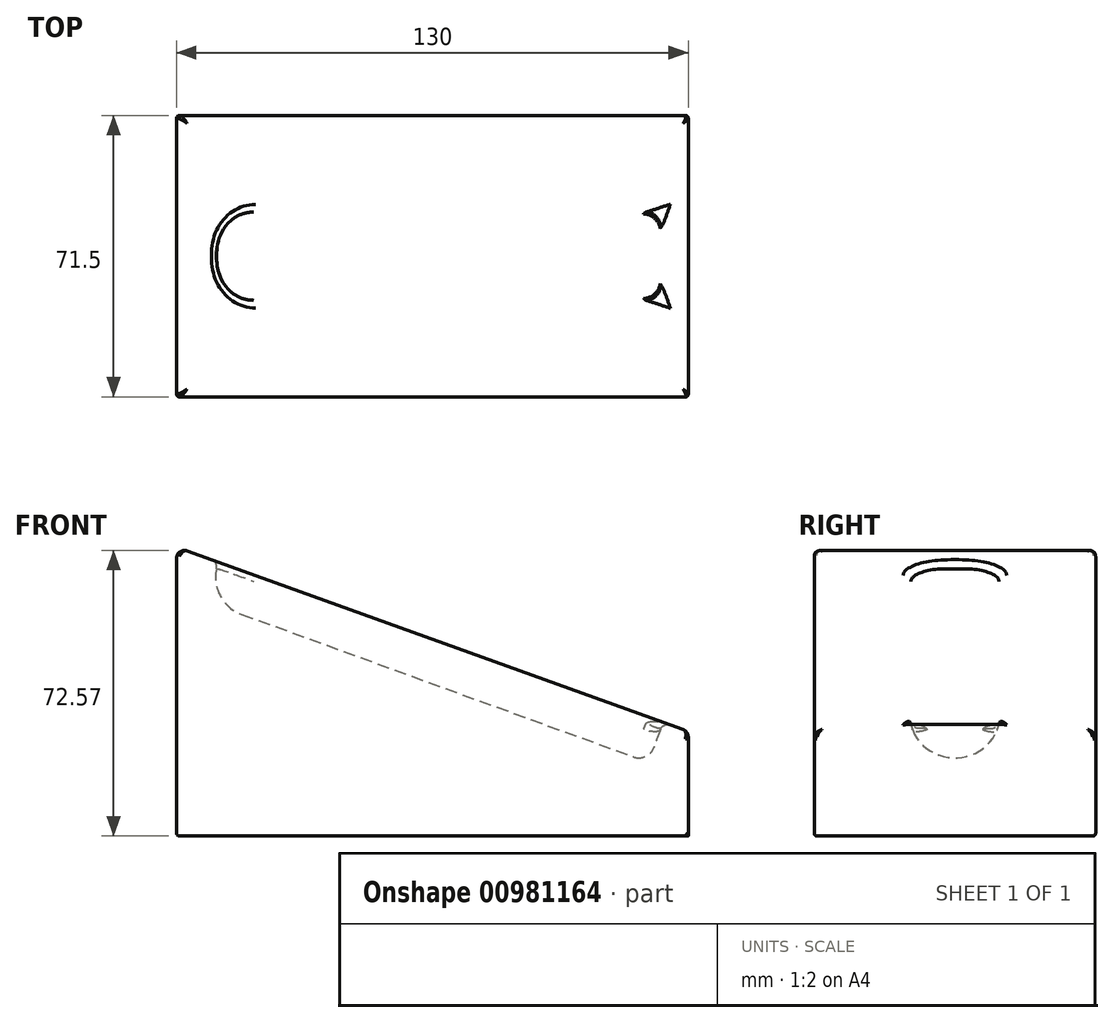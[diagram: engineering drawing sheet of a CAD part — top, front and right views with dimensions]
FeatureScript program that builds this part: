
annotation { "Feature Type Name" : "Feature", "Feature Type Description" : "" }
export const myFeature = defineFeature(function(context is Context, id is Id, definition is map)
    precondition{}
    {
        {
            var Q0;
            Q0=qCreatedBy(makeId("Top.planeOp"),FACE);
            var sketch = newSketch(context, id + "F0", { "sketchPlane" : qUnion([Q0])});
            skLineSegment(sketch, "E0.bottom", {"start": v(0, 0) * mm, "end": v(130, 0) * mm});
            skLineSegment(sketch, "E0.top", {"start": v(0, -71.5) * mm, "end": v(130, -71.5) * mm});
            skLineSegment(sketch, "E0.left", {"start": v(0, 0) * mm, "end": v(0, -71.5) * mm});
            skLineSegment(sketch, "E0.right", {"start": v(130, 0) * mm, "end": v(130, -71.5) * mm});
            skSolve(sketch);
        }
        {
            var Q0;
            Q0=makeQuery(id+"F0.imprint","IMPRINT",FACE,{"disambiguationData":[TD([[makeQuery(id+"F0.imprint","IMPRINT",EDGE,{"derivedFrom":sQuery(id+"F0.wireOp",EDGE,"E0.bottom")}),-1.0]])]});
            extrude(context, id + "F1", {"entities" : qUnion([Q0]), "depth" : 77 * mm, "offsetDistance" : 25 * mm});
        }
        {
            var Q0;
            Q0=makeQuery(id+"F1.opExtrude","SWEPT_FACE",FACE,{"disambiguationData":[OSD([sQuery(id+"F0.wireOp",EDGE,"E0.top")])]});
            var sketch = newSketch(context, id + "F2", { "sketchPlane" : qUnion([Q0])});
            skLineSegment(sketch, "E1", {"start": v(0, 73.42) * mm, "end": v(130, 26.58) * mm});
            skLineSegment(sketch, "E2", {"start": v(130, 26.58) * mm, "end": v(130, 77) * mm});
            skLineSegment(sketch, "E3", {"start": v(130, 77) * mm, "end": v(0, 77) * mm});
            skLineSegment(sketch, "E4", {"start": v(0, 77) * mm, "end": v(0, 73.42) * mm});
            skSolve(sketch);
        }
        {
            var Q0;
            Q0=makeQuery(id+"F2.imprint","IMPRINT",FACE,{"disambiguationData":[TD([[makeQuery(id+"F2.imprint","IMPRINT",EDGE,{"derivedFrom":sQuery(id+"F2.wireOp",EDGE,"E1")}),1.0]])]});
            extrude(context, id + "F3", {"entities" : qUnion([Q0]), "operationType" : NewBodyOperationType.REMOVE, "endBound" : BoundingType.THROUGH_ALL, "oppositeDirection" : true, "depth" : 25 * mm, "offsetDistance" : 25 * mm});
        }
        {
            var Q0;
            Q0=makeQuery(id+"F1.opExtrude","SWEPT_FACE",FACE,{"disambiguationData":[OSD([sQuery(id+"F0.wireOp",EDGE,"E0.right")])]});
            var sketch = newSketch(context, id + "F4", { "sketchPlane" : qUnion([Q0])});
            skArc(sketch, "E5", {"start": v(-47.25, 26.58) * mm, "mid": v(-35.75, 15.08) * mm, "end": v(-24.25, 26.58) * mm});
            skSolve(sketch);
        }
        {
            var Q0;
            Q0 = qSketchRegion(id + "F4", true);
            var Q1;
            {var subQ0=sQuery(id+"F4.wireOp",EDGE,"E5");Q1=makeQuery(id+"F4.imprint","IMPRINT",FACE,{"disambiguationData":[TD([[makeQuery(id+"F4.imprint","IMPRINT",EDGE,{"derivedFrom":subQ0}),1.0]])]});}
            extrude(context, id + "F5", {"entities" : qUnion([Q0, Q1]), "operationType" : NewBodyOperationType.ADD, "depth" : 25 * mm, "offsetDistance" : 25 * mm});
        }
        {
            var Q0;
            Q0=makeQuery(id+"F5.opExtrude","CAP_FACE",FACE,{"disambiguationData":[OSD([sQuery(id+"F0.wireOp",EDGE,"E0.top"),sQuery(id+"F0.wireOp",EDGE,"E0.right"),sQuery(id+"F2.wireOp",EDGE,"E1"),sQuery(id+"F2.wireOp",EDGE,"E2"),sQuery(id+"F4.wireOp",EDGE,"E5")])],"isStart":false});
            extrude(context, id + "F6", {"entities" : qUnion([Q0]), "oppositeDirection" : true, "depth" : 120 * mm, "offsetDistance" : 25 * mm});
        }
        {
            var Q0;
            Q0=makeQuery(id+"F6.opExtrude","SWEPT_BODY",BODY,{"disambiguationData":[OSD([sQuery(id+"F0.wireOp",EDGE,"E0.top"),sQuery(id+"F0.wireOp",EDGE,"E0.right"),sQuery(id+"F2.wireOp",EDGE,"E1"),sQuery(id+"F2.wireOp",EDGE,"E2"),sQuery(id+"F4.wireOp",EDGE,"E5")])]});
            var Q1;
            {var subQ0=sQuery(id+"F2.wireOp",EDGE,"E2");var subQ1=sQuery(id+"F2.wireOp",EDGE,"E1");var subQ2=sQuery(id+"F0.wireOp",EDGE,"E0.right");var subQ3=sQuery(id+"F0.wireOp",EDGE,"E0.top");Q1=makeQuery(id+"F5.boolean.opBoolean","MERGE",EDGE,{"derivedFrom":[makeQuery(id+"F3.boolean.opBoolean","COPY",EDGE,{"derivedFrom":makeQuery(id+"F3.opExtrude","SWEPT_EDGE",EDGE,{"disambiguationData":[OSD([subQ3,subQ2,subQ1,subQ0])]})}),makeQuery(id+"F5.opExtrude","CAP_EDGE",EDGE,{"disambiguationData":[OSD([subQ3,subQ2,subQ1,subQ0])],"isStart":true})]});}
            transform(context, id + "F7", {"entities" : qUnion([Q0]), "transformType" : TransformType.ROTATION, "transformAxis" : qUnion([Q1]), "angle" : 20 * degree, "oppositeDirection" : true, "makeCopy" : false});
        }
        {
            var Q0;
            Q0=makeQuery(id+"F6.opExtrude","SWEPT_BODY",BODY,{"disambiguationData":[OSD([sQuery(id+"F0.wireOp",EDGE,"E0.top"),sQuery(id+"F0.wireOp",EDGE,"E0.right"),sQuery(id+"F2.wireOp",EDGE,"E1"),sQuery(id+"F2.wireOp",EDGE,"E2"),sQuery(id+"F4.wireOp",EDGE,"E5")])]});
            transform(context, id + "F8", {"entities" : qUnion([Q0]), "transformType" : TransformType.TRANSLATION_3D, "dx" : -29.7 * mm, "dy" : 0 * mm, "dz" : 11.5 * mm, "makeCopy" : false});
        }
        {
            var Q0;
            Q0=makeQuery(id+"F6.opExtrude","SWEPT_BODY",BODY,{"disambiguationData":[OSD([sQuery(id+"F0.wireOp",EDGE,"E0.top"),sQuery(id+"F0.wireOp",EDGE,"E0.right"),sQuery(id+"F2.wireOp",EDGE,"E1"),sQuery(id+"F2.wireOp",EDGE,"E2"),sQuery(id+"F4.wireOp",EDGE,"E5")])]});
            var Q1;
            Q1=makeQuery(id+"F1.opExtrude","SWEPT_BODY",BODY,{"disambiguationData":[OSD([sQuery(id+"F0.wireOp",EDGE,"E0.bottom"),sQuery(id+"F0.wireOp",EDGE,"E0.top"),sQuery(id+"F0.wireOp",EDGE,"E0.left"),sQuery(id+"F0.wireOp",EDGE,"E0.right")])]});
            booleanBodies(context, id + "F9", {"operationType" : BooleanOperationType.SUBTRACTION, "tools" : qUnion([Q0]), "targets" : qUnion([Q1])});
        }
        {
            var Q0;
            Q0=makeQuery(id+"F1.opExtrude","CAP_FACE",FACE,{"disambiguationData":[OSD([sQuery(id+"F0.wireOp",EDGE,"E0.bottom"),sQuery(id+"F0.wireOp",EDGE,"E0.top"),sQuery(id+"F0.wireOp",EDGE,"E0.left"),sQuery(id+"F0.wireOp",EDGE,"E0.right")])],"isStart":true});
            var sketch = newSketch(context, id + "F10", { "sketchPlane" : qUnion([Q0])});
            skLineSegment(sketch, "E6.bottom", {"start": v(130, 0) * mm, "end": v(160.74, 0) * mm});
            skLineSegment(sketch, "E6.top", {"start": v(130, 70.96) * mm, "end": v(160.74, 70.96) * mm});
            skLineSegment(sketch, "E6.left", {"start": v(130, 0) * mm, "end": v(130, 70.96) * mm});
            skLineSegment(sketch, "E6.right", {"start": v(160.74, 0) * mm, "end": v(160.74, 70.96) * mm});
            skSolve(sketch);
        }
        {
            var Q0;
            Q0 = qSketchRegion(id + "F10", true);
            extrude(context, id + "F11", {"entities" : qUnion([Q0]), "oppositeDirection" : true, "depth" : 90.6 * mm, "offsetDistance" : 25 * mm, "symmetric" : true});
        }
        {
            var Q0;
            Q0=makeQuery(id+"F11.opExtrude","SWEPT_BODY",BODY,{"disambiguationData":[OSD([sQuery(id+"F10.wireOp",EDGE,"E6.bottom"),sQuery(id+"F10.wireOp",EDGE,"E6.top"),sQuery(id+"F10.wireOp",EDGE,"E6.left"),sQuery(id+"F10.wireOp",EDGE,"E6.right")])]});
            var Q1;
            Q1=makeQuery(id+"F1.opExtrude","SWEPT_BODY",BODY,{"disambiguationData":[OSD([sQuery(id+"F0.wireOp",EDGE,"E0.bottom"),sQuery(id+"F0.wireOp",EDGE,"E0.top"),sQuery(id+"F0.wireOp",EDGE,"E0.left"),sQuery(id+"F0.wireOp",EDGE,"E0.right")])]});
            booleanBodies(context, id + "F12", {"operationType" : BooleanOperationType.SUBTRACTION, "tools" : qUnion([Q0]), "targets" : qUnion([Q1])});
        }
        {
            var Q0;
            Q0=makeQuery(id+"F9.opBoolean","COPY",EDGE,{"derivedFrom":makeQuery(id+"F6.opExtrude","CAP_EDGE",EDGE,{"disambiguationData":[OSD([sQuery(id+"F4.wireOp",EDGE,"E5")])],"isStart":false})});
            fillet(context, id + "F13", {"entities" : qUnion([Q0]), "tangentPropagation" : true, "radius" : 10 * mm, "defaultsChanged" : false, "vertexSettings" : [], "allowEdgeOverflow" : false});
        }
        {
            var Q0;
            Q0=makeQuery(id+"F3.boolean.opBoolean","COPY",FACE,{"derivedFrom":makeQuery(id+"F3.opExtrude","SWEPT_FACE",FACE,{"disambiguationData":[OSD([sQuery(id+"F2.wireOp",EDGE,"E1")])]})});
            fillet(context, id + "F14", {"entities" : qUnion([Q0]), "tangentPropagation" : true, "radius" : 2 * mm, "defaultsChanged" : true, "vertexSettings" : [], "allowEdgeOverflow" : false});
        }
        {
            var Q0;
            Q0=makeQuery(id+"F1.opExtrude","SWEPT_EDGE",EDGE,{"disambiguationData":[OSD([sQuery(id+"F0.wireOp",EDGE,"E0.top"),sQuery(id+"F0.wireOp",EDGE,"E0.right")])]});
            var Q1;
            Q1=makeQuery(id+"F1.opExtrude","SWEPT_EDGE",EDGE,{"disambiguationData":[OSD([sQuery(id+"F0.wireOp",EDGE,"E0.bottom"),sQuery(id+"F0.wireOp",EDGE,"E0.right")])]});
            var Q2;
            Q2=makeQuery(id+"F1.opExtrude","SWEPT_EDGE",EDGE,{"disambiguationData":[OSD([sQuery(id+"F0.wireOp",EDGE,"E0.top"),sQuery(id+"F0.wireOp",EDGE,"E0.left")])]});
            var Q3;
            Q3=makeQuery(id+"F1.opExtrude","SWEPT_EDGE",EDGE,{"disambiguationData":[OSD([sQuery(id+"F0.wireOp",EDGE,"E0.bottom"),sQuery(id+"F0.wireOp",EDGE,"E0.left")])]});
            var Q4;
            Q4=makeQuery(id+"F1.opExtrude","CAP_EDGE",EDGE,{"disambiguationData":[OSD([sQuery(id+"F0.wireOp",EDGE,"E0.right")])],"isStart":true});
            var Q5;
            Q5=makeQuery(id+"F1.opExtrude","CAP_EDGE",EDGE,{"disambiguationData":[OSD([sQuery(id+"F0.wireOp",EDGE,"E0.left")])],"isStart":true});
            var Q6;
            Q6=makeQuery(id+"F1.opExtrude","CAP_EDGE",EDGE,{"disambiguationData":[OSD([sQuery(id+"F0.wireOp",EDGE,"E0.bottom")])],"isStart":true});
            var Q7;
            Q7=makeQuery(id+"F1.opExtrude","CAP_EDGE",EDGE,{"disambiguationData":[OSD([sQuery(id+"F0.wireOp",EDGE,"E0.top")])],"isStart":true});
            fillet(context, id + "F15", {"entities" : qUnion([Q0, Q1, Q2, Q3, Q4, Q5, Q6, Q7]), "tangentPropagation" : true, "radius" : 0.7 * mm, "defaultsChanged" : true, "vertexSettings" : [], "allowEdgeOverflow" : false});
        }
        {
            var Q0;
            Q0=makeQuery(id+"F9.opBoolean","COPY",EDGE,{"derivedFrom":makeQuery(id+"F6.opExtrude","CAP_EDGE",EDGE,{"disambiguationData":[OSD([sQuery(id+"F4.wireOp",EDGE,"E5")])],"isStart":true})});
            fillet(context, id + "F16", {"entities" : qUnion([Q0]), "tangentPropagation" : true, "radius" : 4 * mm, "defaultsChanged" : true, "vertexSettings" : [], "allowEdgeOverflow" : false});
        }
    });
